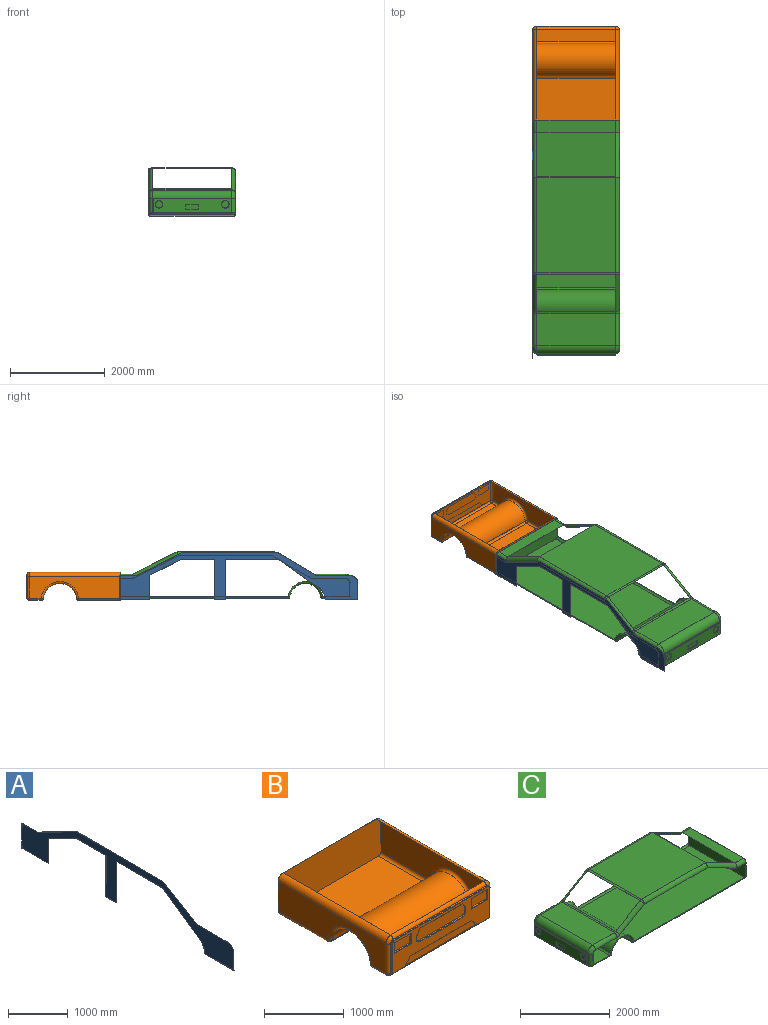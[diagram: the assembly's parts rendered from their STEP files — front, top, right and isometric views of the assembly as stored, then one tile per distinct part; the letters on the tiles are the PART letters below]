
ASSEMBLY  parts=3 mates=2
PART A: 21 faces, bbox 5.1x5029.7x988.2 mm
  f0: plane 5005.91x978mm, normal (1,0,0), area 1411721.9mm2, adj f2,f3,f4,f5,f6,f7,f8,f9
  f1: plane 5016.07x988.16mm, normal (-1,0,0), area 1481974.6mm2, adj f2,f3,f4,f5,f6,f7,f8,f9
  f2: cylinder r=5.08mm len=342.52mm, axis (0,0,1), area 2718.5mm2, adj f0,f1,f3,f4
  f3: torus R=160.66mm, axis (1,0,0), area 2054.3mm2, adj f0,f1,f2,f5
  f4: cylinder r=5.08mm len=693.15mm, axis (0,-1,0), area 5502.4mm2, adj f0,f1,f2,f6
  f5: cylinder r=5.08mm len=709.44mm, axis (0,1,0), area 5654mm2, adj f0,f1,f3,f7
  f6: torus R=333.62mm, axis (1,0,0), area 2935.3mm2, adj f0,f1,f4,f8
  f7: cylinder r=5.08mm len=814.19mm, axis (0,0.86,0.51), area 7515.5mm2, adj f0,f1,f5,f9
  f8: cylinder r=5.08mm len=795.71mm, axis (0,-0.82,-0.58), area 7743.3mm2, adj f0,f1,f6,f10
  f9: cylinder r=5.08mm len=2035.65mm, axis (0,1,0), area 16236.2mm2, adj f0,f1,f7,f11
  f10: cylinder r=5.08mm len=1112.41mm, axis (0,-1,0), area 8842.6mm2, adj f0,f1,f8,f12
  f11: cylinder r=5.08mm len=942.73mm, axis (0,0.89,-0.45), area 8405.9mm2, adj f0,f1,f9,f13
  f12: cylinder r=5.08mm len=851.98mm, axis (0,0,1), area 6758mm2, adj f0,f1,f10,f14
  f13: cylinder r=5.08mm len=358.1mm, axis (0,1,0), area 2836.6mm2, adj f0,f1,f11,f15
  f14: cylinder r=5.08mm len=242.47mm, axis (0,-1,0), area 1905.4mm2, adj f0,f1,f12,f16
  f15: cylinder r=5.08mm len=511.38mm, axis (0,0,-1), area 4051.1mm2, adj f0,f1,f13,f17
  f16: cylinder r=5.08mm len=851.98mm, axis (0,0,-1), area 6758mm2, adj f0,f1,f14,f18
  f17: cylinder r=5.08mm len=623.23mm, axis (0,-1,0), area 4943.9mm2, adj f0,f1,f15,f19
  f18: cylinder r=5.08mm len=693.76mm, axis (0,-1,0), area 5504mm2, adj f0,f1,f16,f20
  f19: cylinder r=5.08mm len=511.4mm, axis (0,-0.01,1), area 4050.4mm2, adj f0,f1,f17,f20
  f20: cylinder r=5.08mm len=673.31mm, axis (0,-0.89,0.45), area 5982.8mm2, adj f0,f1,f18,f19
PART B: 122 faces, bbox 1843.4x1983.2x599 mm
  f0: plane 1298.7x116.78mm, normal (0,-1,0), area 139040.5mm2, adj f17,f80,f81,f82,f99,f105
  f1: plane 1651x2.54mm, normal (0,0,1), area 4193.5mm2, adj f5,f8,f9,f37
  f2: plane 1739.9x249.98mm, normal (0,0,-1), area 434945.5mm2, adj f15,f17,f19,f25
  f3: cylinder r=351.89mm len=1739.9mm, axis (-1,0,0), area 1785849mm2, adj f20,f23,f25,f27
  f4: plane 1739.9x875.66mm, normal (0,0,-1), area 1523563.3mm2, adj f5,f20,f21,f29
  f5: plane 1828.8x591.65mm, normal (0,1,0), area 1077766.5mm2, adj f1,f4,f6,f7,f8,f9,f21,f29
  f6: plane 1913.33x458.3mm, normal (1,0,0), area 665283.8mm2, adj f5,f9,f14,f19,f27,f29
  f7: plane 1913.33x458.3mm, normal (-1,0,0), area 665283.8mm2, adj f5,f8,f10,f15,f21,f23
  f8: cylinder r=88.9mm len=1913.33mm, axis (0,-1,0), area 267184.7mm2, adj f1,f5,f7,f11,f32
  f9: cylinder r=88.9mm len=1913.33mm, axis (0,1,0), area 267184.7mm2, adj f1,f5,f6,f13,f30
  f10: cylinder r=44.45mm len=458.3mm, axis (0,0,-1), area 31999.3mm2, adj f7,f11,f16,f78
  f11: torus R=44.45mm, axis (0,1,0), area 7978.7mm2, adj f8,f10,f12,f77
  f12: cylinder r=44.45mm len=1651mm, axis (-1,0,0), area 115276mm2, adj f11,f13,f31,f76
  f13: torus R=44.45mm, axis (0,1,0), area 7978.7mm2, adj f9,f12,f14,f75
  f14: cylinder r=44.45mm len=458.3mm, axis (0,0,1), area 31999.3mm2, adj f6,f13,f18,f86
  f15: cylinder r=44.45mm len=249.98mm, axis (0,1,0), area 17454.3mm2, adj f2,f7,f16,f24
  f16: sphere r=44.45mm, area 3103.6mm2, adj f10,f15,f17
  f17: cylinder r=44.45mm len=1739.9mm, axis (-1,0,0), area 121483.1mm2, adj f0,f2,f16,f18,f79,f83
  f18: sphere r=44.45mm, area 3103.6mm2, adj f14,f17,f19
  f19: cylinder r=44.45mm len=249.98mm, axis (0,-1,0), area 17454.3mm2, adj f2,f6,f18,f26
  f20: cylinder r=44.45mm len=1739.9mm, axis (-1,0,0), area 112791.3mm2, adj f3,f4,f22,f28
  f21: cylinder r=44.45mm len=875.66mm, axis (0,1,0), area 61140.3mm2, adj f4,f5,f7,f22
  f22: sphere r=44.45mm, area 2881.5mm2, adj f20,f21,f23
  f23: torus R=396.34mm, axis (1,0,0), area 74955.4mm2, adj f3,f7,f22,f24
  f24: sphere r=44.45mm, area 2881.5mm2, adj f15,f23,f25
  f25: cylinder r=44.45mm len=1739.9mm, axis (-1,0,0), area 112791.3mm2, adj f2,f3,f24,f26
  f26: sphere r=44.45mm, area 2881.5mm2, adj f19,f25,f27
  f27: torus R=396.34mm, axis (1,0,0), area 74955.4mm2, adj f3,f6,f26,f28
  f28: sphere r=44.45mm, area 2881.5mm2, adj f20,f27,f29
  f29: cylinder r=44.45mm len=875.66mm, axis (0,-1,0), area 61140.3mm2, adj f4,f5,f6,f28
  f30: plane 1910.79x2.54mm, normal (-1,0,0), area 4853.4mm2, adj f9,f31,f37,f41
  f31: plane 1651x2.54mm, normal (0,1,0), area 4193.5mm2, adj f12,f30,f32,f44
  f32: plane 1910.79x2.54mm, normal (1,0,0), area 4853.4mm2, adj f8,f31,f37,f40
  f33: plane 1739.9x502.75mm, normal (0,1,0), area 873883.9mm2, adj f42,f43,f44,f45,f46,f49
  f34: plane 1739.9x249.98mm, normal (0,0,1), area 434945.5mm2, adj f47,f49,f51,f57
  f35: cylinder r=354.43mm len=1739.9mm, axis (-1,0,0), area 1798739.4mm2, adj f52,f55,f57,f59
  f36: plane 1739.9x873.12mm, normal (0,0,1), area 1519143.9mm2, adj f37,f52,f53,f61
  f37: plane 1823.72x589.11mm, normal (0,-1,0), area 1069975.2mm2, adj f1,f30,f32,f36,f38,f39,f40,f41
  f38: plane 1910.79x458.3mm, normal (-1,0,0), area 664119.7mm2, adj f37,f41,f46,f51,f59,f61
  f39: plane 1910.79x458.3mm, normal (1,0,0), area 664119.7mm2, adj f37,f40,f42,f47,f53,f55
  f40: cylinder r=86.36mm len=1910.79mm, axis (0,-1,0), area 259206.3mm2, adj f32,f37,f39,f43
  f41: cylinder r=86.36mm len=1910.79mm, axis (0,1,0), area 259206.3mm2, adj f30,f37,f38,f45
  f42: cylinder r=41.91mm len=458.3mm, axis (0,0,-1), area 30170.7mm2, adj f33,f39,f43,f48
  f43: torus R=44.45mm, axis (0,1,0), area 7355.5mm2, adj f33,f40,f42,f44
  f44: cylinder r=41.91mm len=1651mm, axis (-1,0,0), area 108688.8mm2, adj f31,f33,f43,f45
  f45: torus R=44.45mm, axis (0,1,0), area 7355.5mm2, adj f33,f41,f44,f46
  f46: cylinder r=41.91mm len=458.3mm, axis (0,0,1), area 30170.7mm2, adj f33,f38,f45,f50
  f47: cylinder r=41.91mm len=249.98mm, axis (0,1,0), area 16456.9mm2, adj f34,f39,f48,f56
  f48: sphere r=41.91mm, area 2759mm2, adj f42,f47,f49
  f49: cylinder r=41.91mm len=1739.9mm, axis (-1,0,0), area 114541.2mm2, adj f33,f34,f48,f50
  f50: sphere r=41.91mm, area 2759mm2, adj f46,f49,f51
  f51: cylinder r=41.91mm len=249.98mm, axis (0,-1,0), area 16456.9mm2, adj f34,f38,f50,f58
  f52: cylinder r=41.91mm len=1739.9mm, axis (-1,0,0), area 106346.1mm2, adj f35,f36,f54,f60
  f53: cylinder r=41.91mm len=873.12mm, axis (0,1,0), area 57479.4mm2, adj f36,f37,f39,f54
  f54: sphere r=41.91mm, area 2561.6mm2, adj f52,f53,f55
  f55: torus R=396.34mm, axis (1,0,0), area 70982.7mm2, adj f35,f39,f54,f56
  f56: sphere r=41.91mm, area 2561.6mm2, adj f47,f55,f57
  f57: cylinder r=41.91mm len=1739.9mm, axis (-1,0,0), area 106346.1mm2, adj f34,f35,f56,f58
  f58: sphere r=41.91mm, area 2561.6mm2, adj f51,f57,f59
  f59: torus R=396.34mm, axis (1,0,0), area 70982.7mm2, adj f35,f38,f58,f60
  f60: sphere r=41.91mm, area 2561.6mm2, adj f52,f59,f61
  f61: cylinder r=41.91mm len=873.12mm, axis (0,-1,0), area 57479.4mm2, adj f36,f37,f38,f60
  f62: plane 151.95x20.32mm, normal (1,0,0), area 3087.6mm2, adj f63,f87,f89,f114
  f63: plane 290.82x20.32mm, normal (0,0,-1), area 5909.4mm2, adj f62,f64,f89,f115
  f64: plane 151.95x20.32mm, normal (-1,0,0), area 3087.6mm2, adj f63,f87,f89,f117
  f65: plane 751.48x20.32mm, normal (0,0,-1), area 15270.1mm2, adj f66,f84,f91,f107
  f66: plane 89.67x57.48mm, normal (-0.84,0,-0.54), area 2164.4mm2, adj f65,f67,f91,f109
  f67: plane 75.88x20.32mm, normal (-1,0,0), area 1541.9mm2, adj f66,f68,f91,f111
  f68: plane 57.48x34.49mm, normal (-0.51,0,0.86), area 1362.2mm2, adj f67,f69,f91,f113
  f69: plane 751.48x20.32mm, normal (0,0,1), area 15270.1mm2, adj f68,f70,f91,f112
  f70: plane 57.48x34.49mm, normal (0.51,0,0.86), area 1362.2mm2, adj f69,f71,f91,f110
  f71: plane 75.88x20.32mm, normal (1,0,0), area 1541.9mm2, adj f70,f84,f91,f108
  f72: plane 151.95x20.32mm, normal (1,0,0), area 3087.6mm2, adj f73,f85,f90,f119
  f73: plane 290.82x20.32mm, normal (0,0,-1), area 5909.4mm2, adj f72,f74,f90,f118
  f74: plane 151.95x20.32mm, normal (-1,0,0), area 3087.6mm2, adj f73,f85,f90,f120
  f75: cylinder r=44.45mm len=44.45mm, axis (0,1,0), area 1418.8mm2, adj f13,f76,f86,f96
  f76: plane 1651x20.32mm, normal (0,0,1), area 33548.3mm2, adj f12,f75,f77,f98
  f77: cylinder r=44.45mm len=44.45mm, axis (0,1,0), area 1418.8mm2, adj f11,f76,f78,f97
  f78: plane 458.3x20.32mm, normal (-1,0,0), area 9312.6mm2, adj f10,f77,f79,f95
  f79: plane 220.6x20.32mm, normal (0,0,-1), area 4482.6mm2, adj f17,f78,f93,f99
  f80: plane 115.06x101.95mm, normal (0.75,0,-0.66), area 3123.9mm2, adj f0,f81,f99,f101
  f81: plane 1087.19x20.32mm, normal (0,0,-1), area 22091.6mm2, adj f0,f80,f82,f102
  f82: plane 115.06x101.95mm, normal (-0.75,0,-0.66), area 3123.9mm2, adj f0,f81,f103,f105
  f83: plane 220.6x20.32mm, normal (0,0,-1), area 4482.6mm2, adj f17,f86,f92,f105
  f84: plane 89.67x57.48mm, normal (0.84,0,-0.54), area 2164.4mm2, adj f65,f71,f91,f106
  f85: plane 290.82x20.32mm, normal (0,0,1), area 5909.4mm2, adj f72,f74,f90,f121
  f86: plane 458.3x20.32mm, normal (1,0,0), area 9312.6mm2, adj f14,f75,f83,f94
  f87: plane 290.82x20.32mm, normal (0,0,1), area 5909.4mm2, adj f62,f64,f89,f116
  f88: plane 1729.74x492.59mm, normal (0,-1,0), area 437781.6mm2, adj f92,f93,f94,f95,f96,f97,f98,f101
  f89: plane 290.82x151.95mm, normal (0,-1,0), area 44190.1mm2, adj f62,f63,f64,f87
  f90: plane 290.82x151.95mm, normal (0,-1,0), area 44190.1mm2, adj f72,f73,f74,f85
  f91: plane 866.45x200.04mm, normal (0,-1,0), area 166190mm2, adj f65,f66,f67,f68,f69,f70,f71,f84
  f92: cylinder r=5.08mm len=220.6mm, axis (-1,0,0), area 1745.6mm2, adj f83,f88,f94,f104
  f93: cylinder r=5.08mm len=220.6mm, axis (-1,0,0), area 1745.6mm2, adj f79,f88,f95,f100
  f94: cylinder r=5.08mm len=458.3mm, axis (0,0,-1), area 3642.3mm2, adj f86,f88,f92,f96
  f95: cylinder r=5.08mm len=458.3mm, axis (0,0,1), area 3642.3mm2, adj f78,f88,f93,f97
  f96: torus R=39.37mm, axis (0,-1,0), area 534mm2, adj f75,f88,f94,f98
  f97: torus R=39.37mm, axis (0,-1,0), area 534mm2, adj f77,f88,f95,f98
  f98: cylinder r=5.08mm len=1651mm, axis (1,0,0), area 13174.4mm2, adj f76,f88,f96,f97
  f99: cylinder r=5.08mm len=20.32mm, axis (0,1,0), area 87.3mm2, adj f0,f79,f80,f100
  f100: sphere r=5.08mm, area 21.8mm2, adj f93,f99,f101
  f101: cylinder r=5.08mm len=120.14mm, axis (-0.66,0,-0.75), area 1233.4mm2, adj f80,f88,f100,f102
  f102: cylinder r=5.08mm len=1091.76mm, axis (-1,0,0), area 8688.6mm2, adj f81,f88,f101,f103
  f103: cylinder r=5.08mm len=120.14mm, axis (-0.66,0,0.75), area 1233.4mm2, adj f82,f88,f102,f104
  f104: sphere r=5.08mm, area 21.8mm2, adj f92,f103,f105
  f105: cylinder r=5.08mm len=20.32mm, axis (0,-1,0), area 87.3mm2, adj f0,f82,f83,f104
  f106: cylinder r=5.08mm len=96.01mm, axis (-0.54,0,-0.84), area 862.3mm2, adj f84,f88,f107,f108
  f107: cylinder r=5.08mm len=757.04mm, axis (-1,0,0), area 6012.7mm2, adj f65,f88,f106,f109
  f108: cylinder r=5.08mm len=80.24mm, axis (0,0,-1), area 618.1mm2, adj f71,f88,f106,f110
  f109: cylinder r=5.08mm len=96.01mm, axis (-0.54,0,0.84), area 862.3mm2, adj f66,f88,f107,f111
  f110: cylinder r=5.08mm len=63.77mm, axis (0.86,0,-0.51), area 547.4mm2, adj f70,f88,f108,f112
  f111: cylinder r=5.08mm len=80.24mm, axis (0,0,1), area 618.1mm2, adj f67,f88,f109,f113
  f112: cylinder r=5.08mm len=754.3mm, axis (1,0,0), area 6004.7mm2, adj f69,f88,f110,f113
  f113: cylinder r=5.08mm len=63.77mm, axis (0.86,0,0.51), area 547.4mm2, adj f68,f88,f111,f112
  f114: cylinder r=5.08mm len=162.11mm, axis (0,0,-1), area 1242mm2, adj f62,f88,f115,f116
  f115: cylinder r=5.08mm len=300.98mm, axis (-1,0,0), area 2350.1mm2, adj f63,f88,f114,f117
  f116: cylinder r=5.08mm len=300.98mm, axis (1,0,0), area 2350.1mm2, adj f87,f88,f114,f117
  f117: cylinder r=5.08mm len=162.11mm, axis (0,0,1), area 1242mm2, adj f64,f88,f115,f116
  f118: cylinder r=5.08mm len=300.98mm, axis (-1,0,0), area 2350.1mm2, adj f73,f88,f119,f120
  f119: cylinder r=5.08mm len=162.11mm, axis (0,0,-1), area 1242mm2, adj f72,f88,f118,f121
  f120: cylinder r=5.08mm len=162.11mm, axis (0,0,1), area 1242mm2, adj f74,f88,f118,f121
  f121: cylinder r=5.08mm len=300.98mm, axis (1,0,0), area 2350.1mm2, adj f85,f88,f119,f120
PART C: 178 faces, bbox 4948.4x1843.4x988.2 mm
  f0: cylinder r=328.54mm len=1739.9mm, axis (0,1,0), area 1608925.3mm2, adj f32,f37,f41,f44
  f1: plane 3533.68x1739.9mm, normal (0,0,-1), area 6148249.4mm2, adj f2,f31,f35,f41
  f2: plane 1828.8x511.38mm, normal (1,0,0), area 930965.4mm2, adj f1,f3,f9,f10,f11,f15,f31,f35
  f3: plane 1651x263.79mm, normal (0,0,1), area 435524.6mm2, adj f2,f11,f15,f76
  f4: plane 1651x5mm, normal (0.45,0,0.89), area 9265.3mm2, adj f5,f12,f18,f109
  f5: plane 2011.3x1651mm, normal (0,0,1), area 3320660.3mm2, adj f4,f14,f21,f22
  f6: plane 1651x683.7mm, normal (0,0,1), area 1128790.6mm2, adj f7,f19,f25,f28
  f7: cylinder r=165.74mm len=1651mm, axis (0,1,0), area 429821.7mm2, adj f6,f16,f29,f46
  f8: plane 1739.9x608.82mm, normal (0,0,-1), area 1058436.7mm2, adj f33,f34,f36,f38,f39,f44
  f9: plane 378.03x2.54mm, normal (0,-1,0), area 960.2mm2, adj f2,f15,f31,f107
  f10: plane 378.03x2.54mm, normal (0,1,0), area 960.2mm2, adj f2,f11,f35,f107
  f11: cylinder r=88.9mm len=285.06mm, axis (-1,0,0), area 37916.6mm2, adj f2,f3,f10,f12,f84
  f12: cylinder r=88.9mm len=998.55mm, axis (-0.89,0,0.45), area 147103.7mm2, adj f4,f11,f14,f78,f85
  f13: cylinder r=88.9mm len=298.07mm, axis (0,0,-1), area 41623.8mm2, adj f16,f38,f47,f91
  f14: cylinder r=88.9mm len=2011.3mm, axis (-1,0,0), area 279786.6mm2, adj f5,f12,f17,f86
  f15: cylinder r=88.9mm len=285.06mm, axis (1,0,0), area 37916.6mm2, adj f2,f3,f9,f18,f100
  f16: torus R=76.84mm, axis (0,-1,0), area 29268.8mm2, adj f7,f13,f19,f90
  f17: sphere r=88.9mm, area 4225.4mm2, adj f14,f20,f21
  f18: cylinder r=88.9mm len=998.55mm, axis (0.89,0,-0.45), area 147103.7mm2, adj f4,f15,f22,f77,f99
  f19: cylinder r=88.9mm len=683.7mm, axis (-1,0,0), area 95474.6mm2, adj f6,f16,f23,f89
  f20: cylinder r=88.9mm len=813.8mm, axis (-0.86,0,-0.51), area 124721.9mm2, adj f17,f23,f81,f87
  f21: cylinder r=88.9mm len=1651mm, axis (0,1,0), area 78472.5mm2, adj f5,f17,f24,f82
  f22: cylinder r=88.9mm len=2011.3mm, axis (1,0,0), area 279786.6mm2, adj f5,f18,f24,f98
  f23: torus R=177.8mm, axis (0,-1,0), area 9049.2mm2, adj f19,f20,f25,f88
  f24: sphere r=88.9mm, area 4225.4mm2, adj f21,f22,f26
  f25: cylinder r=88.9mm len=1651mm, axis (0,-1,0), area 78472.5mm2, adj f6,f23,f27,f80
  f26: cylinder r=88.9mm len=813.8mm, axis (0.86,0,0.51), area 124721.9mm2, adj f24,f27,f79,f97
  f27: torus R=177.8mm, axis (0,-1,0), area 9049.2mm2, adj f25,f26,f28,f96
  f28: cylinder r=88.9mm len=683.7mm, axis (1,0,0), area 95474.6mm2, adj f6,f27,f29,f95
  f29: torus R=76.84mm, axis (0,-1,0), area 29268.8mm2, adj f7,f28,f30,f94
  f30: cylinder r=88.9mm len=298.07mm, axis (0,0,1), area 41623.8mm2, adj f29,f34,f56,f104
  f31: cylinder r=44.45mm len=3533.68mm, axis (-1,0,0), area 246728.2mm2, adj f1,f2,f9,f42,f101
  f32: torus R=372.99mm, axis (0,-1,0), area 67740.2mm2, adj f0,f42,f45,f102
  f33: cylinder r=44.45mm len=564.37mm, axis (-1,0,0), area 39405.3mm2, adj f8,f34,f45,f103
  f34: torus R=44.45mm, axis (0,0,-1), area 7978.7mm2, adj f8,f30,f33,f36
  f35: cylinder r=44.45mm len=3533.68mm, axis (1,0,0), area 246728.2mm2, adj f1,f2,f10,f40,f83
  f36: cylinder r=44.45mm len=1651mm, axis (0,1,0), area 115276mm2, adj f8,f34,f38,f48
  f37: torus R=372.99mm, axis (0,-1,0), area 67740.2mm2, adj f0,f40,f43,f93
  f38: torus R=44.45mm, axis (0,0,-1), area 7978.7mm2, adj f8,f13,f36,f39
  f39: cylinder r=44.45mm len=564.37mm, axis (1,0,0), area 39405.3mm2, adj f8,f38,f43,f92
  f40: sphere r=44.45mm, area 2780.6mm2, adj f35,f37,f41
  f41: cylinder r=44.45mm len=1739.9mm, axis (0,1,0), area 108840.8mm2, adj f0,f1,f40,f42
  f42: sphere r=44.45mm, area 2780.6mm2, adj f31,f32,f41
  f43: sphere r=44.45mm, area 2780.6mm2, adj f37,f39,f44
  f44: cylinder r=44.45mm len=1739.9mm, axis (0,1,0), area 108840.8mm2, adj f0,f8,f43,f45
  f45: sphere r=44.45mm, area 2780.6mm2, adj f32,f33,f44
  f46: plane 1651x20.32mm, normal (0,0,1), area 33548.3mm2, adj f7,f47,f56,f74
  f47: plane 298.07x20.32mm, normal (0,1,0), area 6056.8mm2, adj f13,f46,f48,f72
  f48: plane 1651x20.32mm, normal (0,0,-1), area 33548.3mm2, adj f36,f47,f56,f73
  f49: cylinder r=25.4mm len=25.4mm, axis (1,0,0), area 810.7mm2, adj f50,f58,f62,f67
  f50: plane 51.84x20.32mm, normal (0,-1,0), area 1053.4mm2, adj f49,f51,f62,f65
  f51: cylinder r=25.4mm len=25.4mm, axis (1,0,0), area 810.7mm2, adj f50,f52,f62,f64
  f52: plane 224.9x20.32mm, normal (0,0,-1), area 4569.9mm2, adj f51,f53,f62,f66
  f53: cylinder r=25.4mm len=25.4mm, axis (1,0,0), area 810.7mm2, adj f52,f54,f62,f68
  f54: plane 51.84x20.32mm, normal (0,1,0), area 1053.4mm2, adj f53,f55,f62,f70
  f55: cylinder r=25.4mm len=25.4mm, axis (1,0,0), area 810.7mm2, adj f54,f58,f62,f71
  f56: plane 298.07x20.32mm, normal (0,-1,0), area 6056.8mm2, adj f30,f46,f48,f75
  f57: cylinder r=76.86mm len=153.72mm, axis (1,0,0), area 12266.6mm2, adj f60,f63
  f58: plane 224.9x20.32mm, normal (0,0,1), area 4569.9mm2, adj f49,f55,f62,f69
  f59: cylinder r=76.86mm len=153.72mm, axis (1,0,0), area 12266.6mm2, adj f60,f61
  f60: plane 1640.84x287.91mm, normal (-1,0,0), area 403848.8mm2, adj f57,f59,f64,f65,f66,f67,f68,f69
  f61: plane 153.72x153.72mm, normal (-1,0,0), area 18559.7mm2, adj f59
  f62: plane 275.7x102.64mm, normal (-1,0,0), area 27744.6mm2, adj f49,f50,f51,f52,f53,f54,f55,f58
  f63: plane 153.72x153.72mm, normal (-1,0,0), area 18559.7mm2, adj f57
  f64: torus R=30.48mm, axis (-1,0,0), area 341.5mm2, adj f51,f60,f65,f66
  f65: cylinder r=5.08mm len=51.84mm, axis (0,0,-1), area 413.7mm2, adj f50,f60,f64,f67
  f66: cylinder r=5.08mm len=224.9mm, axis (0,1,0), area 1794.6mm2, adj f52,f60,f64,f68
  f67: torus R=30.48mm, axis (-1,0,0), area 341.5mm2, adj f49,f60,f65,f69
  f68: torus R=30.48mm, axis (-1,0,0), area 341.5mm2, adj f53,f60,f66,f70
  f69: cylinder r=5.08mm len=224.9mm, axis (0,-1,0), area 1794.6mm2, adj f58,f60,f67,f71
  f70: cylinder r=5.08mm len=51.84mm, axis (0,0,1), area 413.7mm2, adj f54,f60,f68,f71
  f71: torus R=30.48mm, axis (-1,0,0), area 341.5mm2, adj f55,f60,f69,f70
  f72: cylinder r=5.08mm len=298.07mm, axis (0,0,1), area 2349mm2, adj f47,f60,f73,f74
  f73: cylinder r=5.08mm len=1651mm, axis (0,1,0), area 13144.9mm2, adj f48,f60,f72,f75
  f74: cylinder r=5.08mm len=1651mm, axis (0,-1,0), area 13144.9mm2, adj f46,f60,f72,f75
  f75: cylinder r=5.08mm len=298.07mm, axis (0,0,-1), area 2349mm2, adj f56,f60,f73,f74
  f76: plane 1651x5mm, normal (-0.45,0,-0.89), area 9265.3mm2, adj f3,f77,f78,f108
  f77: plane 944.96x476.79mm, normal (0,1,0), area 2675.7mm2, adj f18,f76,f109,f117,f120
  f78: plane 944.96x476.79mm, normal (0,-1,0), area 2675.7mm2, adj f12,f76,f109,f113,f114
  f79: plane 769.8x457.28mm, normal (0,1,0), area 2268.6mm2, adj f26,f80,f82,f128
  f80: plane 1651x2.19mm, normal (0.86,0,0.51), area 4193.5mm2, adj f25,f79,f81,f127
  f81: plane 769.8x457.28mm, normal (0,-1,0), area 2268.6mm2, adj f20,f80,f82,f122
  f82: plane 1651x2.19mm, normal (-0.86,0,-0.51), area 4193.5mm2, adj f21,f79,f81,f123
  f83: plane 3531.14x2.54mm, normal (0,0,1), area 8969.1mm2, adj f35,f93,f107,f137
  f84: plane 282.52x2.54mm, normal (0,0,-1), area 717.6mm2, adj f11,f85,f107,f113
  f85: plane 939.35x476.79mm, normal (-0.45,0,-0.89), area 2675.7mm2, adj f12,f84,f86,f114
  f86: plane 1990.03x2.54mm, normal (0,0,-1), area 5054.7mm2, adj f14,f85,f87,f116
  f87: plane 768.5x455.09mm, normal (0.51,0,-0.86), area 2268.6mm2, adj f20,f86,f88,f122
  f88: cylinder r=177.8mm len=90.6mm, axis (0,-1,0), area 241.5mm2, adj f23,f87,f89,f125
  f89: plane 683.7x2.54mm, normal (0,0,-1), area 1736.6mm2, adj f19,f88,f90,f121
  f90: cylinder r=76.84mm len=76.84mm, axis (0,-1,0), area 306.6mm2, adj f16,f89,f91,f118
  f91: plane 298.07x2.54mm, normal (1,0,0), area 757.1mm2, adj f13,f90,f92,f115
  f92: plane 564.37x2.54mm, normal (0,0,1), area 1433.5mm2, adj f39,f91,f93,f141
  f93: cylinder r=372.99mm len=736.03mm, axis (0,-1,0), area 2666.6mm2, adj f37,f83,f92,f139
  f94: cylinder r=76.84mm len=76.84mm, axis (0,-1,0), area 306.6mm2, adj f29,f95,f104,f131
  f95: plane 683.7x2.54mm, normal (0,0,-1), area 1736.6mm2, adj f28,f94,f96,f130
  f96: cylinder r=177.8mm len=90.6mm, axis (0,-1,0), area 241.5mm2, adj f27,f95,f97,f129
  f97: plane 768.5x455.09mm, normal (0.51,0,-0.86), area 2268.6mm2, adj f26,f96,f98,f128
  f98: plane 1990.03x2.54mm, normal (0,0,-1), area 5054.7mm2, adj f22,f97,f99,f124
  f99: plane 939.35x476.79mm, normal (-0.45,0,-0.89), area 2675.7mm2, adj f18,f98,f100,f120
  f100: plane 282.52x2.54mm, normal (0,0,-1), area 717.6mm2, adj f15,f99,f107,f117
  f101: plane 3531.14x2.54mm, normal (0,0,1), area 8969.1mm2, adj f31,f102,f107,f133
  f102: cylinder r=372.99mm len=736.03mm, axis (0,-1,0), area 2666.6mm2, adj f32,f101,f103,f134
  f103: plane 564.37x2.54mm, normal (0,0,1), area 1433.5mm2, adj f33,f102,f104,f135
  f104: plane 298.07x2.54mm, normal (1,0,0), area 757.1mm2, adj f30,f94,f103,f132
  f105: cylinder r=331.08mm len=1739.9mm, axis (0,1,0), area 1621364.2mm2, adj f134,f139,f143,f146
  f106: plane 3531.14x1739.9mm, normal (0,0,1), area 6143830mm2, adj f107,f133,f137,f143
  f107: plane 1828.8x506.3mm, normal (-1,0,0), area 921308.7mm2, adj f9,f10,f83,f84,f100,f101,f106,f108
  f108: plane 1651x256.25mm, normal (0,0,-1), area 423069.1mm2, adj f76,f107,f113,f117
  f109: plane 2016.31x1651mm, normal (0,0,-1), area 3328922.3mm2, adj f4,f77,f78,f116,f123,f124
  f110: plane 1651x683.7mm, normal (0,0,-1), area 1128790.6mm2, adj f111,f121,f127,f130
  f111: cylinder r=163.2mm len=1651mm, axis (0,1,0), area 427415.3mm2, adj f110,f115,f118,f131,f132,f148,f149,f158
  f112: plane 1739.9x608.82mm, normal (0,0,1), area 1058436.7mm2, adj f135,f136,f138,f140,f141,f146
  f113: cylinder r=86.36mm len=282.52mm, axis (-1,0,0), area 36541.2mm2, adj f78,f84,f107,f108,f114
  f114: cylinder r=86.36mm len=996.86mm, axis (-0.89,0,0.45), area 142900.7mm2, adj f78,f85,f113,f116
  f115: cylinder r=86.36mm len=301.56mm, axis (0,0,-1), area 41185.1mm2, adj f91,f111,f118,f138,f140,f149,f150
  f116: cylinder r=86.36mm len=2010.69mm, axis (-1,0,0), area 271740.2mm2, adj f86,f109,f114,f119
  f117: cylinder r=86.36mm len=282.52mm, axis (1,0,0), area 36541.2mm2, adj f77,f100,f107,f108,f120
  f118: torus R=76.84mm, axis (0,-1,0), area 28088mm2, adj f90,f111,f115,f121
  f119: sphere r=86.36mm, area 3987.4mm2, adj f116,f122,f123
  f120: cylinder r=86.36mm len=996.86mm, axis (0.89,0,-0.45), area 142900.7mm2, adj f77,f99,f117,f124
  f121: cylinder r=86.36mm len=683.7mm, axis (-1,0,0), area 92746.8mm2, adj f89,f110,f118,f125
  f122: cylinder r=86.36mm len=812.51mm, axis (-0.86,0,-0.51), area 121158.4mm2, adj f81,f87,f119,f125
  f123: cylinder r=86.36mm len=1651mm, axis (0,1,0), area 76230.4mm2, adj f82,f109,f119,f126
  f124: cylinder r=86.36mm len=2010.69mm, axis (1,0,0), area 271740.2mm2, adj f98,f109,f120,f126
  f125: torus R=177.8mm, axis (0,-1,0), area 8907.9mm2, adj f88,f121,f122,f127
  f126: sphere r=86.36mm, area 3987.4mm2, adj f123,f124,f128
  f127: cylinder r=91.44mm len=1651mm, axis (0,-1,0), area 80714.6mm2, adj f80,f110,f125,f129
  f128: cylinder r=86.36mm len=812.51mm, axis (0.86,0,0.51), area 121158.4mm2, adj f79,f97,f126,f129
  f129: torus R=177.8mm, axis (0,-1,0), area 8907.9mm2, adj f96,f127,f128,f130
  f130: cylinder r=86.36mm len=683.7mm, axis (1,0,0), area 92746.8mm2, adj f95,f110,f129,f131
  f131: torus R=76.84mm, axis (0,-1,0), area 28088mm2, adj f94,f111,f130,f132
  f132: cylinder r=86.36mm len=298.07mm, axis (0,0,1), area 41176.2mm2, adj f104,f111,f131,f136,f138,f150,f158
  f133: cylinder r=41.91mm len=3531.14mm, axis (-1,0,0), area 232462.3mm2, adj f101,f106,f107,f144
  f134: torus R=372.99mm, axis (0,-1,0), area 64169mm2, adj f102,f105,f144,f147
  f135: cylinder r=41.91mm len=564.37mm, axis (-1,0,0), area 37153.6mm2, adj f103,f112,f136,f147
  f136: torus R=44.45mm, axis (0,0,-1), area 7355.5mm2, adj f112,f132,f135,f138
  f137: cylinder r=41.91mm len=3531.14mm, axis (1,0,0), area 232462.3mm2, adj f83,f106,f107,f142
  f138: cylinder r=41.91mm len=1658.29mm, axis (0,1,0), area 112894.1mm2, adj f112,f115,f132,f136,f140,f150
  f139: torus R=372.99mm, axis (0,-1,0), area 64169mm2, adj f93,f105,f142,f145
  f140: torus R=44.45mm, axis (0,0,-1), area 7355.5mm2, adj f112,f115,f138,f141
  f141: cylinder r=41.91mm len=564.37mm, axis (1,0,0), area 37153.6mm2, adj f92,f112,f140,f145
  f142: sphere r=41.91mm, area 2471.9mm2, adj f137,f139,f143
  f143: cylinder r=41.91mm len=1739.9mm, axis (0,1,0), area 102621.3mm2, adj f105,f106,f142,f144
  f144: sphere r=41.91mm, area 2471.9mm2, adj f133,f134,f143
  f145: sphere r=41.91mm, area 2471.9mm2, adj f139,f141,f146
  f146: cylinder r=41.91mm len=1739.9mm, axis (0,1,0), area 102621.3mm2, adj f105,f112,f145,f147
  f147: sphere r=41.91mm, area 2471.9mm2, adj f134,f135,f146
  f148: plane 1645.92x22.88mm, normal (0,0,-1), area 37658.3mm2, adj f111,f149,f158,f176
  f149: plane 299.02x22.9mm, normal (0,-1,0), area 6708.9mm2, adj f111,f115,f148,f150,f174
  f150: plane 1658.29x22.94mm, normal (0,0,1), area 37753.2mm2, adj f115,f132,f138,f149,f158,f175
  f151: cylinder r=27.94mm len=27.94mm, axis (1,0,0), area 1003.3mm2, adj f152,f160,f164,f169
  f152: plane 51.84x22.86mm, normal (0,1,0), area 1185.1mm2, adj f151,f153,f164,f167
  f153: cylinder r=27.94mm len=27.94mm, axis (1,0,0), area 1003.3mm2, adj f152,f154,f164,f166
  f154: plane 224.9x22.86mm, normal (0,0,1), area 5141.2mm2, adj f153,f155,f164,f168
  f155: cylinder r=27.94mm len=27.94mm, axis (1,0,0), area 1003.3mm2, adj f154,f156,f164,f170
  f156: plane 51.84x22.86mm, normal (0,-1,0), area 1185.1mm2, adj f155,f157,f164,f172
  f157: cylinder r=27.94mm len=27.94mm, axis (1,0,0), area 1003.3mm2, adj f156,f160,f164,f173
  f158: plane 292.99x22.9mm, normal (0,1,0), area 6708.7mm2, adj f111,f132,f148,f150,f177
  f159: cylinder r=79.4mm len=158.8mm, axis (1,0,0), area 12672mm2, adj f162,f165
  f160: plane 224.9x22.86mm, normal (0,0,-1), area 5141.2mm2, adj f151,f157,f164,f171
  f161: cylinder r=79.4mm len=158.8mm, axis (1,0,0), area 12672mm2, adj f162,f163
  f162: plane 1640.84x287.91mm, normal (1,0,0), area 401355mm2, adj f159,f161,f166,f167,f168,f169,f170,f171
  f163: plane 158.8x158.8mm, normal (1,0,0), area 19806.6mm2, adj f161
  f164: plane 280.78x107.72mm, normal (1,0,0), area 29576.1mm2, adj f151,f152,f153,f154,f155,f156,f157,f160
  f165: plane 158.8x158.8mm, normal (1,0,0), area 19806.6mm2, adj f159
  f166: torus R=30.48mm, axis (-1,0,0), area 180.9mm2, adj f153,f162,f167,f168
  f167: cylinder r=2.54mm len=51.84mm, axis (0,0,-1), area 206.8mm2, adj f152,f162,f166,f169
  f168: cylinder r=2.54mm len=224.9mm, axis (0,1,0), area 897.3mm2, adj f154,f162,f166,f170
  f169: torus R=30.48mm, axis (-1,0,0), area 180.9mm2, adj f151,f162,f167,f171
  f170: torus R=30.48mm, axis (-1,0,0), area 180.9mm2, adj f155,f162,f168,f172
  f171: cylinder r=2.54mm len=224.9mm, axis (0,-1,0), area 897.3mm2, adj f160,f162,f169,f173
  f172: cylinder r=2.54mm len=51.84mm, axis (0,0,1), area 206.8mm2, adj f156,f162,f170,f173
  f173: torus R=30.48mm, axis (-1,0,0), area 180.9mm2, adj f157,f162,f171,f172
  f174: cylinder r=2.54mm len=292.99mm, axis (0,0,1), area 1161.6mm2, adj f149,f162,f175,f176
  f175: cylinder r=2.54mm len=1645.92mm, axis (0,1,0), area 6559.6mm2, adj f150,f162,f174,f177
  f176: cylinder r=2.54mm len=1645.92mm, axis (0,-1,0), area 6559.6mm2, adj f148,f162,f174,f177
  f177: cylinder r=2.54mm len=292.99mm, axis (0,0,-1), area 1161.6mm2, adj f158,f162,f175,f176
PLACE A t=(0,49.85,0)mm
PLACE B rot(axis=(0,0,1),180deg) t=(1833.88,3144.18,96.8)mm
PLACE C rot(axis=(0,0,1),90deg) t=(5.08,552.78,-302.58)mm
MATE fastened B.f5 <-> C.f2  axis (0,-1,0) through (919.48,2881.36,-199.67)mm
MATE fastened B.f6 <-> A.f0  axis (-1,0,0) through (5.08,2881.36,-221.25)mm
